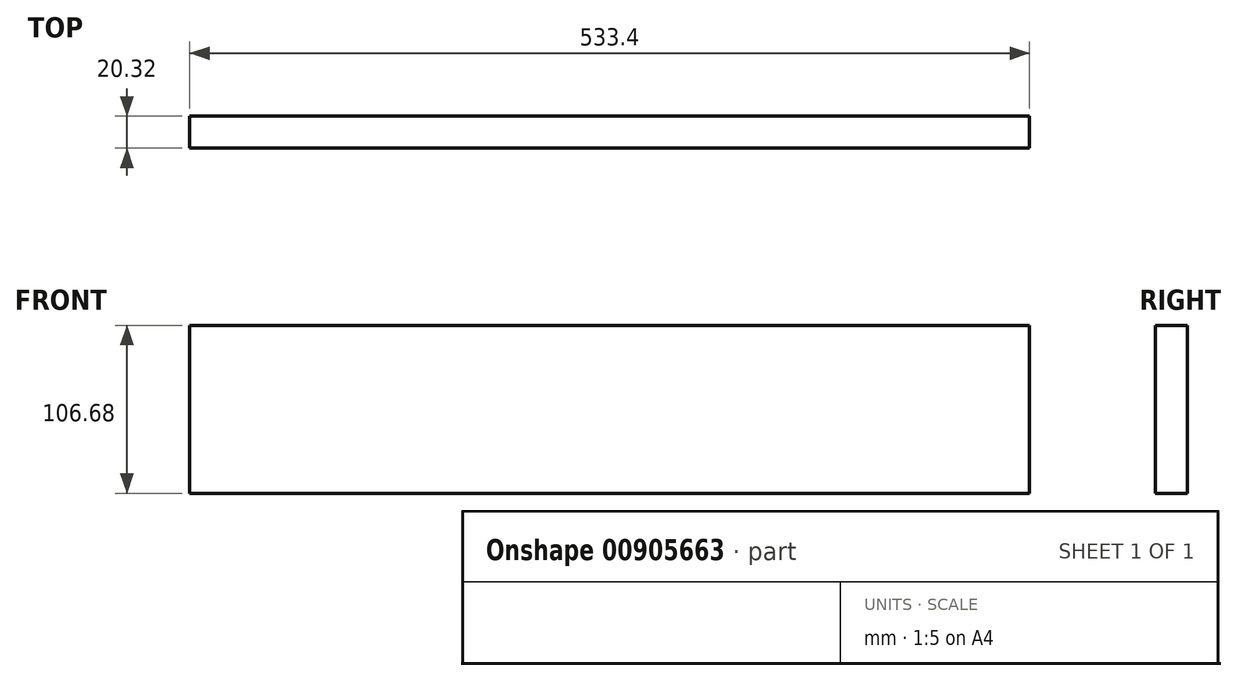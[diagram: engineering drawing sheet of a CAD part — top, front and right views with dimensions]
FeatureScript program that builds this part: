
annotation { "Feature Type Name" : "Feature", "Feature Type Description" : "" }
export const myFeature = defineFeature(function(context is Context, id is Id, definition is map)
    precondition{}
    {
        {
            var Q0;
            Q0=qCreatedBy(makeId("Front.planeOp"),FACE);
            var sketch = newSketch(context, id + "F0", { "sketchPlane" : qUnion([Q0])});
            skLineSegment(sketch, "E0.bottom", {"start": v(266.7, 53.34) * mm, "end": v(-266.7, 53.34) * mm});
            skLineSegment(sketch, "E0.top", {"start": v(266.7, -53.34) * mm, "end": v(-266.7, -53.34) * mm});
            skLineSegment(sketch, "E0.left", {"start": v(266.7, 53.34) * mm, "end": v(266.7, -53.34) * mm});
            skLineSegment(sketch, "E0.right", {"start": v(-266.7, 53.34) * mm, "end": v(-266.7, -53.34) * mm});
            skPoint(sketch, "E0.middle", {"position": v(0, 0) * mm});
            skSolve(sketch);
        }
        {
            var Q0;
            Q0 = qSketchRegion(id + "F0", true);
            extrude(context, id + "F1", {"entities" : qUnion([Q0]), "depth" : 20.32 * mm, "offsetDistance" : 25.4 * mm});
        }
    });
